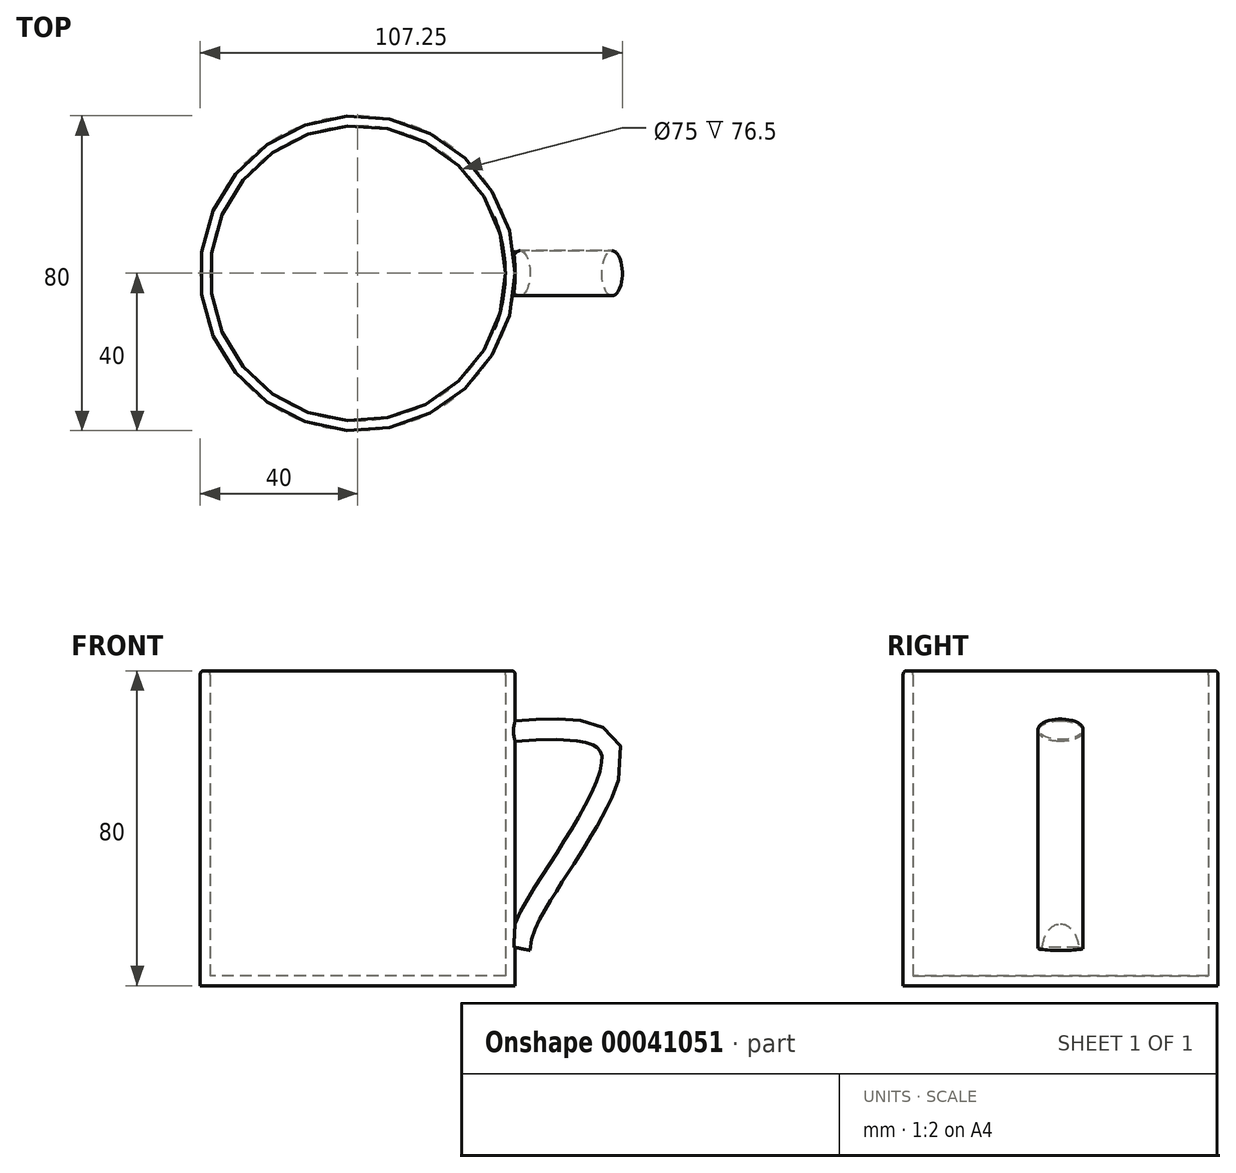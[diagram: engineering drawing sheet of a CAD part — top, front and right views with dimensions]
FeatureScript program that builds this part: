
annotation { "Feature Type Name" : "Feature", "Feature Type Description" : "" }
export const myFeature = defineFeature(function(context is Context, id is Id, definition is map)
    precondition{}
    {
        {
            var Q0;
            Q0=qCreatedBy(makeId("Top.planeOp"),FACE);
            var sketch = newSketch(context, id + "F0", { "sketchPlane" : qUnion([Q0])});
            skCircle(sketch, "E0", {"center": v(0, 0) * mm, "radius": 40 * mm});
            skSolve(sketch);
        }
        {
            var Q0;
            Q0=makeQuery(id+"F0.imprint","IMPRINT",FACE,{"disambiguationData":[TD([[makeQuery(id+"F0.imprint","IMPRINT",EDGE,{"derivedFrom":sQuery(id+"F0.wireOp",EDGE,"E0")}),1.0]])]});
            extrude(context, id + "F1", {"entities" : qUnion([Q0]), "depth" : 80 * mm});
        }
        {
            var Q0;
            Q0=makeQuery(id+"F1.opExtrude","CAP_FACE",FACE,{"disambiguationData":[OSD([sQuery(id+"F0.wireOp",EDGE,"E0")])],"isStart":false});
            shell(context, id + "F2", {"entities" : qUnion([Q0]), "thickness" : 2.5 * mm});
        }
        {
            var Q0;
            Q0=qCreatedBy(makeId("Right.planeOp"),FACE);
            cPlane(context, id + "F3", {"entities" : qUnion([Q0]), "cplaneType" : CPlaneType.OFFSET, "offset" : 39 * mm, "width" : 150 * mm, "height" : 150 * mm});
        }
        {
            var Q0;
            Q0=qCreatedBy(makeId("Front.planeOp"),FACE);
            var sketch = newSketch(context, id + "F4", { "sketchPlane" : qUnion([Q0])});
            skFitSpline(sketch, "E1", {"points": [v(38.42, 64.03) * mm, v(63.94, 59.2) * mm, v(44.09, 19.51) * mm, v(40.69, 9.59) * mm], "startDerivative": vector(106.12, 7.32) * mm, "endDerivative": vector(-4.39, -34.25) * mm});
            skSolve(sketch);
        }
        {
            var Q0;
            Q0=qCreatedBy(id+"F3.planeOp",FACE);
            var sketch = newSketch(context, id + "F5", { "sketchPlane" : qUnion([Q0])});
            skEllipse(sketch, "E2", {"center": v(0, 64.62) * mm, "majorRadius": 5.72 * mm, "minorRadius": 2.61 * mm, "majorAxis": v(1, 0)});
            skSolve(sketch);
        }
        {
            var Q0;
            Q0 = qSketchRegion(id + "F5", true);
            var Q1;
            Q1 = qConstructionFilter(qBodyType(qCreatedBy(id + "F4" ,EDGE), BodyType.WIRE), ConstructionObject.NO);
            sweep(context, id + "F6", {"operationType" : NewBodyOperationType.ADD, "profiles" : qUnion([Q0]), "path" : qUnion([Q1])});
        }
        {
            var Q0;
            Q0=makeQuery(id+"F1.opExtrude","CAP_EDGE",EDGE,{"disambiguationData":[OSD([sQuery(id+"F0.wireOp",EDGE,"E0")])],"isStart":false});
            var Q1;
            {var subQ0=sQuery(id+"F0.wireOp",EDGE,"E0");Q1=makeQuery(id+"F2.opShell","OFFSET_EDGE",EDGE,{"disambiguationData":[OSD([subQ0]),TDD([makeQuery(id+"F1.opExtrude","CAP_EDGE",EDGE,{"disambiguationData":[OSD([subQ0])],"isStart":false})])]});}
            fillet(context, id + "F7", {"entities" : qUnion([Q0, Q1]), "radius" : 1 * mm, "rho" : 0.5, "crossSection" : FilletCrossSection.CONIC, "allowEdgeOverflow" : false});
        }
    });
